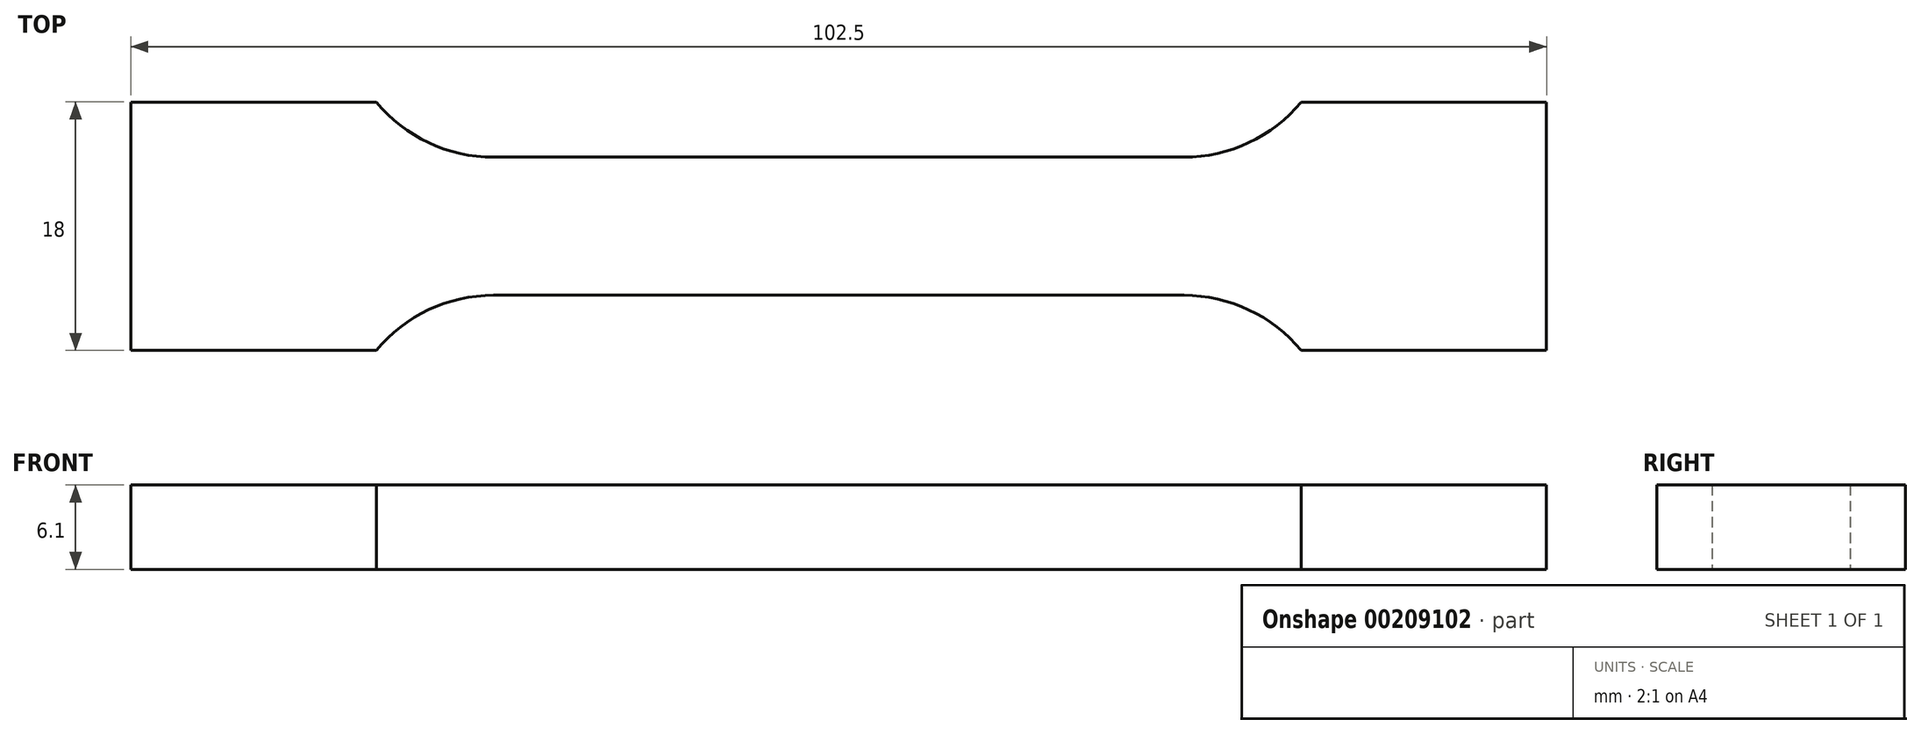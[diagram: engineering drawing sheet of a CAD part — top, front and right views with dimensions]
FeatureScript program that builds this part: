
annotation { "Feature Type Name" : "Feature", "Feature Type Description" : "" }
export const myFeature = defineFeature(function(context is Context, id is Id, definition is map)
    precondition{}
    {
        {
            var Q0;
            Q0=qCreatedBy(makeId("Top.planeOp"),FACE);
            var sketch = newSketch(context, id + "F0", { "sketchPlane" : qUnion([Q0])});
            skPoint(sketch, "E0.MirrorP", {"position": v(-20.12, 23.85) * mm});
            skArc(sketch, "E1.MirrorCS", {"start": v(4.88, 28.85) * mm, "mid": v(9.57, 29.9) * mm, "end": v(13.36, 32.85) * mm});
            skLineSegment(sketch, "E2.MirrorCS", {"start": v(-71.37, 14.85) * mm, "end": v(-53.6, 14.85) * mm});
            skLineSegment(sketch, "E3.MirrorCS", {"start": v(4.88, 18.85) * mm, "end": v(-45.12, 18.85) * mm});
            skLineSegment(sketch, "E4.MirrorCS", {"start": v(-71.37, 32.85) * mm, "end": v(-71.37, 14.85) * mm});
            skLineSegment(sketch, "E5.MirrorCS", {"start": v(31.13, 32.85) * mm, "end": v(31.13, 14.85) * mm});
            skArc(sketch, "E6.MirrorCS", {"start": v(-45.12, 28.85) * mm, "mid": v(-49.81, 29.9) * mm, "end": v(-53.6, 32.85) * mm});
            skLineSegment(sketch, "E7.MirrorCS", {"start": v(13.36, 14.85) * mm, "end": v(31.13, 14.85) * mm});
            skLineSegment(sketch, "E8.MirrorCS", {"start": v(4.88, 28.85) * mm, "end": v(-45.12, 28.85) * mm});
            skLineSegment(sketch, "E9.MirrorCS", {"start": v(-71.37, 32.85) * mm, "end": v(-53.6, 32.85) * mm});
            skLineSegment(sketch, "E10.MirrorCS", {"start": v(13.36, 32.85) * mm, "end": v(31.13, 32.85) * mm});
            skArc(sketch, "E11.MirrorCS", {"start": v(-45.12, 18.85) * mm, "mid": v(-49.81, 17.8) * mm, "end": v(-53.6, 14.85) * mm});
            skArc(sketch, "E12.MirrorCS", {"start": v(4.88, 18.85) * mm, "mid": v(9.57, 17.8) * mm, "end": v(13.36, 14.85) * mm});
            skSolve(sketch);
        }
        {
            var Q0;
            Q0=makeQuery(id+"F0.imprint","IMPRINT",FACE,{"disambiguationData":[TD([[makeQuery(id+"F0.imprint","IMPRINT",EDGE,{"derivedFrom":sQuery(id+"F0.wireOp",EDGE,"E1.MirrorCS")}),-1.0]])]});
            extrude(context, id + "F1", {"entities" : qUnion([Q0]), "depth" : 6.1 * mm, "symmetric" : true});
        }
    });
